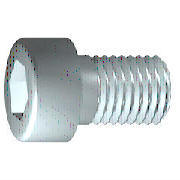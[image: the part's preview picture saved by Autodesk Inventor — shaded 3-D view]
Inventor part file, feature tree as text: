
AUTODESK INVENTOR PART (.ipt)
format: ipt  version: 2017 (Build 210142000, 142)  size: 187,904 bytes
history: native  units: mm (DEFAULTED — no unit token found)
features: sketch x2, other x1, extrude x1, plane x1, fillet x1
ambient origin geometry x7: Origin, YZ Plane, XY Plane, X Axis, Y Axis, Z Axis, Center Point
bodies: Solid1 (feature_tree)
feature tree (6):
  other  "Corps"
  extrude  "Rainure"  Depth=18.75mm
  plane  "Work Plane1"
  fillet  "Fillet2"  Radius=0.306825mm
  sketch  "Esquisse1"
  sketch  "Esquisse2"
